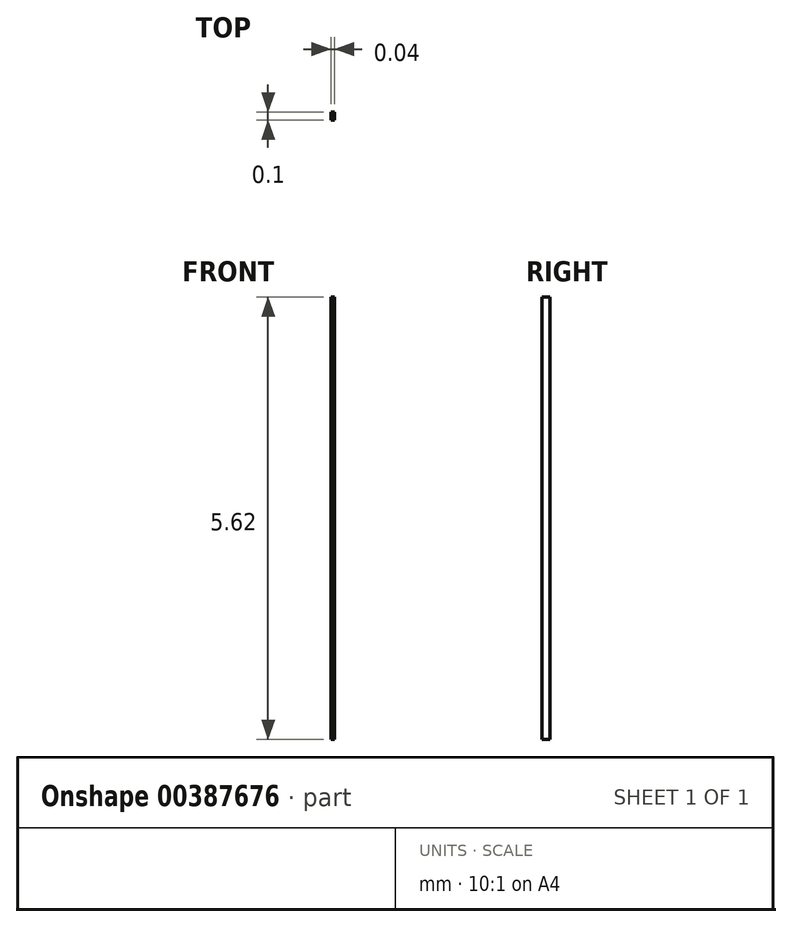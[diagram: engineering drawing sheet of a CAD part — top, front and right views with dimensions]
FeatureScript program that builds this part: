
annotation { "Feature Type Name" : "Feature", "Feature Type Description" : "" }
export const myFeature = defineFeature(function(context is Context, id is Id, definition is map)
    precondition{}
    {
        {
            var Q0;
            Q0=qCreatedBy(makeId("Right.planeOp"),FACE);
            var sketch = newSketch(context, id + "F0", { "sketchPlane" : qUnion([Q0])});
            skLineSegment(sketch, "E0.bottom", {"start": v(0.05, -2.8) * mm, "end": v(-0.05, -2.8) * mm});
            skLineSegment(sketch, "E0.top", {"start": v(0.05, 2.8) * mm, "end": v(-0.05, 2.8) * mm});
            skLineSegment(sketch, "E0.left", {"start": v(0.05, -2.8) * mm, "end": v(0.05, 2.8) * mm});
            skLineSegment(sketch, "E0.right", {"start": v(-0.05, -2.8) * mm, "end": v(-0.05, 2.8) * mm});
            skPoint(sketch, "E0.middle", {"position": v(0, 0) * mm});
            skSolve(sketch);
        }
        {
            var Q0;
            Q0 = qSketchRegion(id + "F0", true);
            extrude(context, id + "F1", {"entities" : qUnion([Q0]), "endBound" : BoundingType.SYMMETRIC, "depth" : 0.05 * mm});
        }
    });
